# Revit family: 3-61-6 Cirro Pendant
name_source: partatom
category: Generic Models
units: mm (PartAtom-declared; Revit-internal decimal feet)

## family parameters
Always vertical = No
Can host rebar = No
Cut with Voids When Loaded = No
Part Type = Undefined
Room Calculation Point = No
Round Connector Dimension = Use Diameter
Shared = Yes

## types (2) — shared parameters
Color = 3000 K
Lamp = LED Array
Main Diffuser = Oxygen Lighting - Diffuser - Matte White Acrylic
Manufacturer = Oxygen - Lighting & Fans
Model = 3-61-6 Cirro Pendant
Pendant Heigth = 10.63 "
References = Ref. 3 = 120 V / Ref. 37 = 277 V
URL = www.oxygenlighting.com
Voltage Input = 120 V or 277 V - 50/60 Hz
Wattage = 95 W
Wattage Comments = 95.0 W at 120 V
Wires Heigth = 18.46 "
zero-valued in all types: Default Elevation

## per-type parameters (varying)
| type | Metal Finish |
| 3-61-15 / Black - Matte White Acrylic | Oxygen Lighting - Metal Finish - 15 - Black |
| 3-61-6 / White - Matte White Acrylic | Oxygen Lighting - Metal Finish - 06 - White |

## geometry (parser evidence)
native form markers: Blend x2, Extrusion x1, Sweep x4
no freeform markers — native parametric forms only
